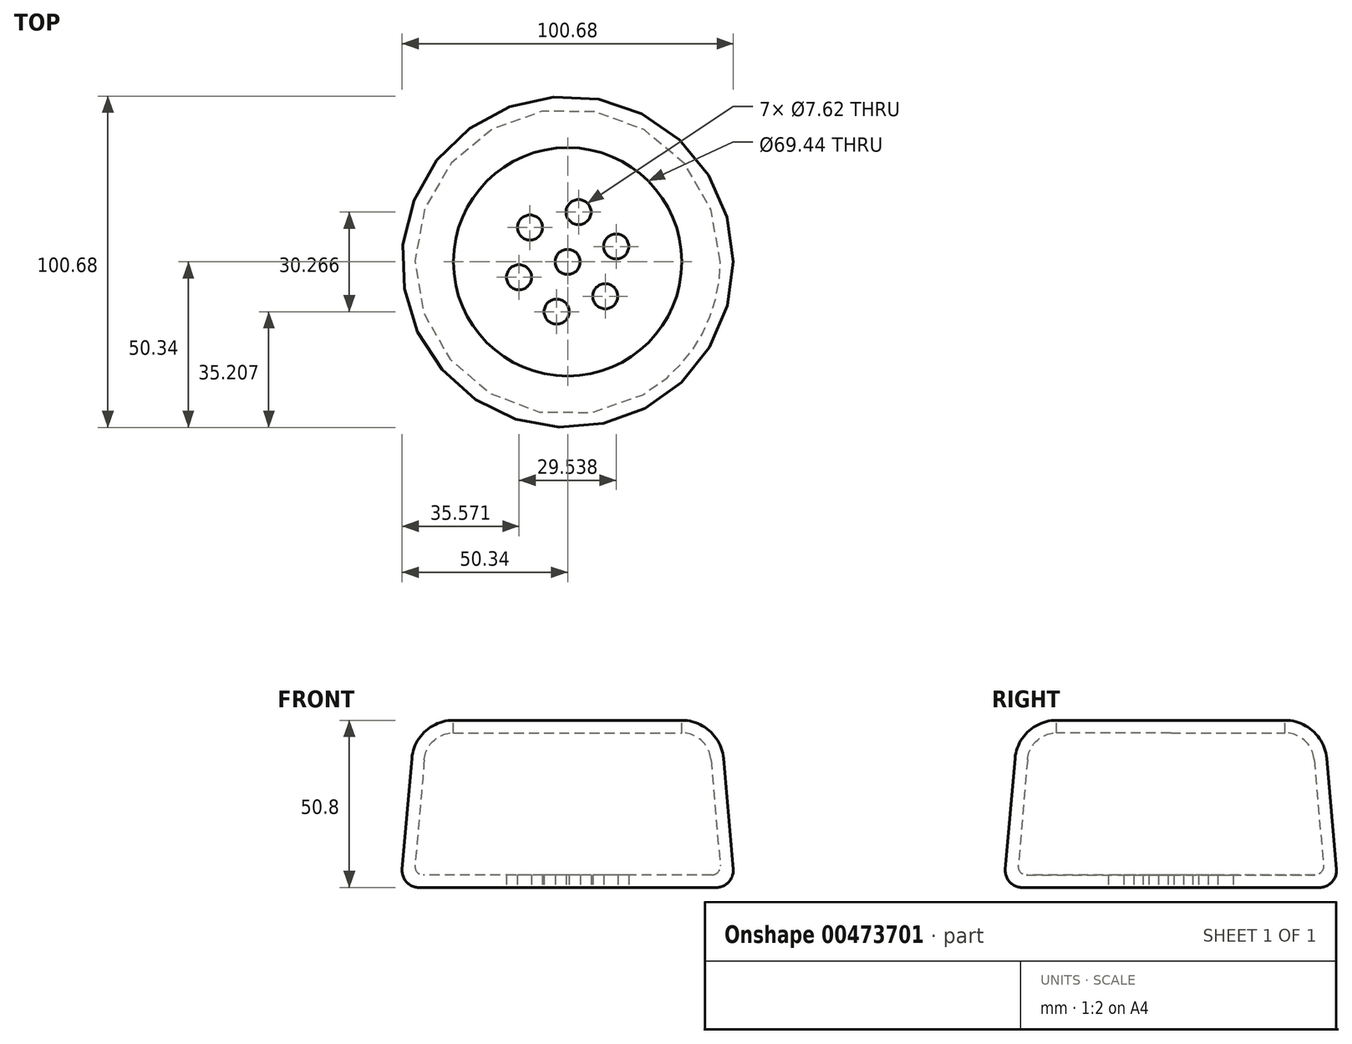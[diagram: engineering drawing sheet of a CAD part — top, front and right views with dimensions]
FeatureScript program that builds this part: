
annotation { "Feature Type Name" : "Feature", "Feature Type Description" : "" }
export const myFeature = defineFeature(function(context is Context, id is Id, definition is map)
    precondition{}
    {
        {
            var Q0;
            Q0=qCreatedBy(makeId("Top.planeOp"),FACE);
            var sketch = newSketch(context, id + "F0", { "sketchPlane" : qUnion([Q0])});
            skCircle(sketch, "E0", {"center": v(0, 0) * mm, "radius": 50.8 * mm});
            skSolve(sketch);
        }
        {
            var Q0;
            Q0=makeQuery(id+"F0.imprint","IMPRINT",FACE,{"disambiguationData":[TD([[makeQuery(id+"F0.imprint","IMPRINT",EDGE,{"derivedFrom":sQuery(id+"F0.wireOp",EDGE,"E0")}),1.0]])]});
            extrude(context, id + "F1", {"entities" : qUnion([Q0]), "depth" : 50.8 * mm, "hasDraft" : true, "draftAngle" : 5 * degree, "draftPullDirection" : true});
        }
        {
            var Q0;
            Q0=makeQuery(id+"F1.opExtrude","CAP_EDGE",EDGE,{"disambiguationData":[OSD([sQuery(id+"F0.wireOp",EDGE,"E0")])],"isStart":false});
            fillet(context, id + "F2", {"entities" : qUnion([Q0]), "radius" : 12.7 * mm, "tangentPropagation" : true, "allowEdgeOverflow" : false});
        }
        {
            var Q0;
            Q0=makeQuery(id+"F1.opExtrude","CAP_FACE",FACE,{"disambiguationData":[OSD([sQuery(id+"F0.wireOp",EDGE,"E0")])],"isStart":false});
            shell(context, id + "F3", {"entities" : qUnion([Q0]), "thickness" : 3.8 * mm});
        }
        {
            var Q0;
            {var subQ0=sQuery(id+"F0.wireOp",EDGE,"E0");Q0=makeQuery(id+"F3.opShell","OFFSET_EDGE",EDGE,{"disambiguationData":[OSD([subQ0]),TDD([makeQuery(id+"F1.opExtrude","CAP_EDGE",EDGE,{"disambiguationData":[OSD([subQ0])],"isStart":true})])]});}
            fillet(context, id + "F4", {"entities" : qUnion([Q0]), "radius" : 2.54 * mm, "tangentPropagation" : true, "allowEdgeOverflow" : false});
        }
        {
            var Q0;
            Q0=qCreatedBy(makeId("Top.planeOp"),FACE);
            var sketch = newSketch(context, id + "F5", { "sketchPlane" : qUnion([Q0])});
            skCircle(sketch, "E1.cCircle", {"center": v(0, 0) * mm, "radius": 13.42 * mm, "construction": true});
            skLineSegment(sketch, "E1.0", {"start": v(3.33, 15.13) * mm, "end": v(14.77, 4.69) * mm});
            skLineSegment(sketch, "E1.1", {"start": v(14.77, 4.69) * mm, "end": v(11.44, -10.45) * mm});
            skLineSegment(sketch, "E1.2", {"start": v(11.44, -10.45) * mm, "end": v(-3.33, -15.13) * mm});
            skLineSegment(sketch, "E1.3", {"start": v(-3.33, -15.13) * mm, "end": v(-14.77, -4.69) * mm});
            skLineSegment(sketch, "E1.4", {"start": v(-14.77, -4.69) * mm, "end": v(-11.44, 10.45) * mm});
            skLineSegment(sketch, "E1.5", {"start": v(-11.44, 10.45) * mm, "end": v(3.33, 15.13) * mm});
            skPoint(sketch, "E1.0.midPoint", {"position": v(9.05, 9.9) * mm});
            skSolve(sketch);
        }
        {
            var Q0;
            Q0=sQuery(id+"F5.wireOp",VERTEX,"E1.0.start");
            var Q1;
            Q1=sQuery(id+"F5.wireOp",VERTEX,"E1.5.start");
            var Q2;
            Q2=sQuery(id+"F5.wireOp",VERTEX,"E1.3.end");
            var Q3;
            Q3=sQuery(id+"F5.wireOp",VERTEX,"E1.3.start");
            var Q4;
            Q4=sQuery(id+"F5.wireOp",VERTEX,"E1.2.start");
            var Q5;
            Q5=sQuery(id+"F5.wireOp",VERTEX,"E1.1.start");
            var Q6;
            Q6=sQuery(id+"F5.wireOp",VERTEX,"E1.cCircle.center");
            var Q7;
            Q7=makeQuery(id+"F1.opExtrude","SWEPT_BODY",BODY,{"disambiguationData":[OSD([sQuery(id+"F0.wireOp",EDGE,"E0")])]});
            hole(context, id + "F6", {"style" : HoleStyle.SIMPLE, "endStyle" : HoleEndStyle.THROUGH, "oppositeDirection" : true, "holeDiameter" : 7.62 * mm, "isTappedThrough" : true, "tappedDepth" : 12.7 * mm, "tapClearance" : 3, "locations" : qUnion([Q0, Q1, Q2, Q3, Q4, Q5, Q6]), "scope" : qUnion([Q7])});
        }
        {
            var Q0;
            Q0=makeQuery(id+"F1.opExtrude","CAP_EDGE",EDGE,{"disambiguationData":[OSD([sQuery(id+"F0.wireOp",EDGE,"E0")])],"isStart":true});
            fillet(context, id + "F7", {"entities" : qUnion([Q0]), "radius" : 5.08 * mm, "tangentPropagation" : true, "allowEdgeOverflow" : false});
        }
    });
